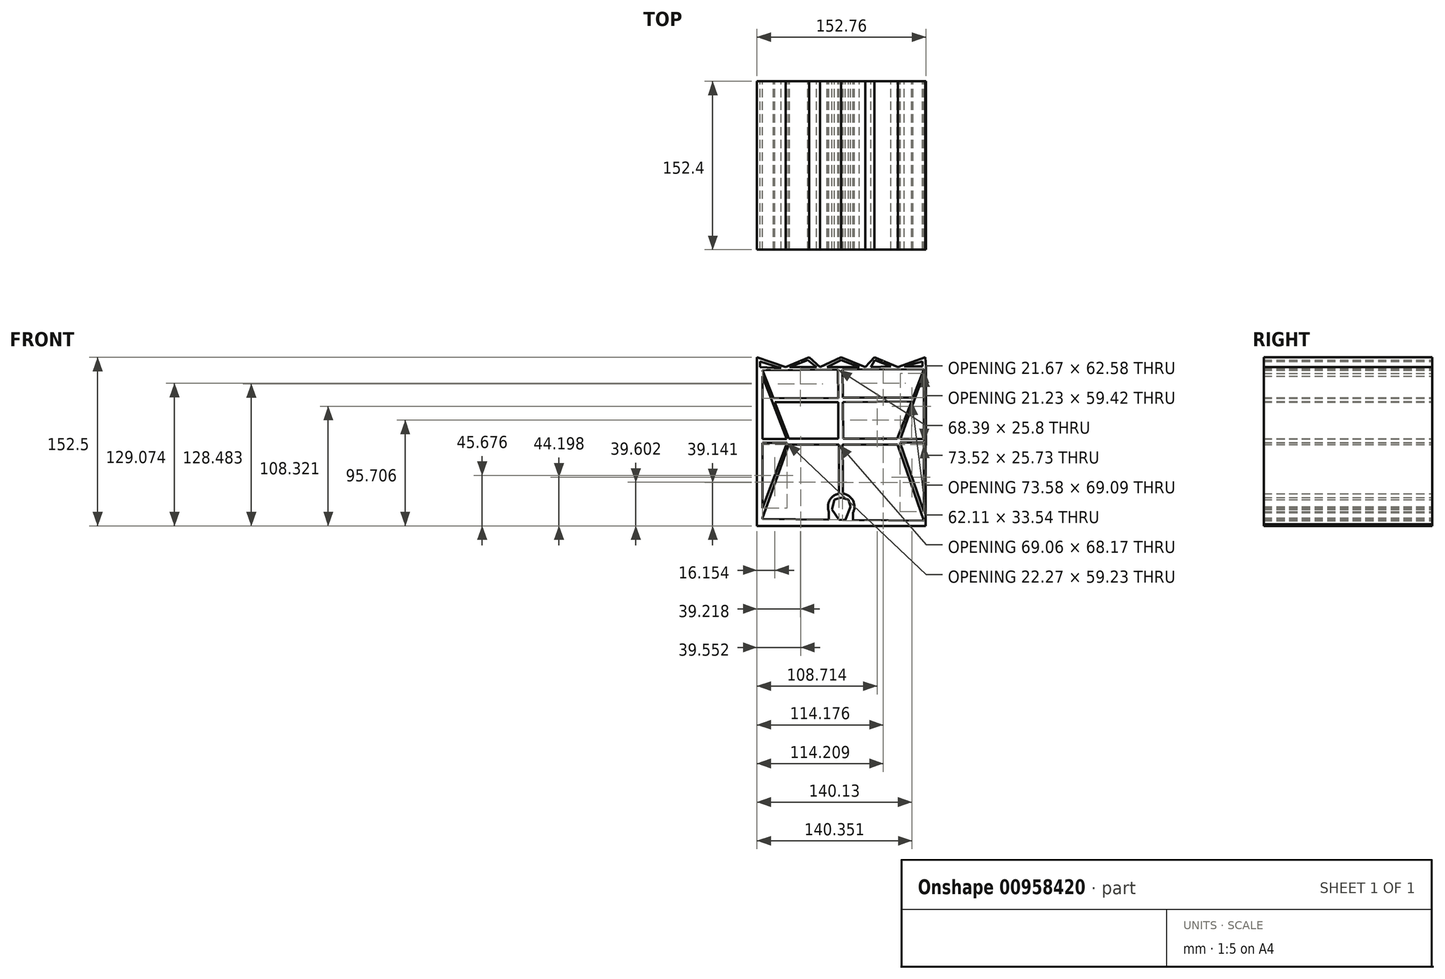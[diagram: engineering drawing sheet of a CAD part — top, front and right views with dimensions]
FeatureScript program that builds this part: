
annotation { "Feature Type Name" : "Feature", "Feature Type Description" : "" }
export const myFeature = defineFeature(function(context is Context, id is Id, definition is map)
    precondition{}
    {
        {
            var Q0;
            Q0=qCreatedBy(makeId("Front.planeOp"),FACE);
            var sketch = newSketch(context, id + "F0", { "sketchPlane" : qUnion([Q0])});
            skLineSegment(sketch, "E0", {"start": v(-71.15, 59.1) * mm, "end": v(-71.15, 2.17) * mm});
            skLineSegment(sketch, "E1", {"start": v(-71.15, -70.3) * mm, "end": v(-11.18, -70.94) * mm});
            skLineSegment(sketch, "E2", {"start": v(74.8, 65.48) * mm, "end": v(1.28, 64.96) * mm});
            skLineSegment(sketch, "E3", {"start": v(-71.15, 64.44) * mm, "end": v(-61.46, 39.21) * mm});
            skLineSegment(sketch, "E4", {"start": v(-47.38, -2.77) * mm, "end": v(-71.15, -69.26) * mm});
            skLineSegment(sketch, "E5", {"start": v(74.8, 65.48) * mm, "end": v(65.02, 39.75) * mm});
            skLineSegment(sketch, "E6", {"start": v(50.87, -2.77) * mm, "end": v(74.8, -71.87) * mm});
            skLineSegment(sketch, "E7", {"start": v(-71.15, 59.1) * mm, "end": v(-49.28, 2.17) * mm});
            skLineSegment(sketch, "E8", {"start": v(-48.88, -1.17) * mm, "end": v(-71.15, -60.4) * mm});
            skLineSegment(sketch, "E9", {"start": v(74.8, 61.57) * mm, "end": v(53.56, 2.17) * mm});
            skLineSegment(sketch, "E10", {"start": v(53.12, -0.97) * mm, "end": v(74.8, -63.55) * mm});
            skPoint(sketch, "E11.start.orphan", {"position": v(-69.1, -63.55) * mm});
            skLineSegment(sketch, "E12.trimOffspring", {"start": v(-71.15, -69.26) * mm, "end": v(-71.15, -70.3) * mm});
            skLineSegment(sketch, "E13.trimOffspring", {"start": v(74.8, -63.55) * mm, "end": v(74.8, -1) * mm});
            skLineSegment(sketch, "E14", {"start": v(-76.17, 67.36) * mm, "end": v(-76.17, -76.46) * mm});
            skLineSegment(sketch, "E15", {"start": v(-76.17, -76.46) * mm, "end": v(76.3, -76.46) * mm});
            skLineSegment(sketch, "E16", {"start": v(76.45, -74.92) * mm, "end": v(76.3, -76.46) * mm});
            skLineSegment(sketch, "E17", {"start": v(76.45, -74.92) * mm, "end": v(76.59, 67.36) * mm});
            skPoint(sketch, "E18.end.orphan", {"position": v(74.8, -68.33) * mm});
            skArc(sketch, "E19", {"start": v(10.66, -64.64) * mm, "mid": v(10.6, -53.5) * mm, "end": v(1.41, -47.21) * mm});
            skLineSegment(sketch, "E20", {"start": v(-2.09, -47.31) * mm, "end": v(-2.09, -30.61) * mm});
            skLineSegment(sketch, "E21", {"start": v(1.41, -30.61) * mm, "end": v(1.41, -47.21) * mm});
            skLineSegment(sketch, "E22", {"start": v(-2.09, -70.94) * mm, "end": v(-8.25, -61.78) * mm});
            skLineSegment(sketch, "E23", {"start": v(-8.25, -61.78) * mm, "end": v(-6.15, -52.84) * mm});
            skLineSegment(sketch, "E24", {"start": v(-6.15, -52.84) * mm, "end": v(0, -50.7) * mm});
            skLineSegment(sketch, "E25", {"start": v(0, -50.7) * mm, "end": v(6.43, -52.84) * mm});
            skLineSegment(sketch, "E26", {"start": v(6.43, -52.84) * mm, "end": v(8.6, -59.12) * mm});
            skLineSegment(sketch, "E27", {"start": v(8.6, -59.12) * mm, "end": v(3.63, -71.1) * mm});
            skLineSegment(sketch, "E28.trimOffspring", {"start": v(10.66, -71.18) * mm, "end": v(74.8, -71.87) * mm});
            skArc(sketch, "E29.trimOffspring", {"start": v(-2.09, -47.31) * mm, "mid": v(-10.46, -53.24) * mm, "end": v(-11.18, -63.47) * mm});
            skLineSegment(sketch, "E30", {"start": v(-71.15, 2.17) * mm, "end": v(-49.28, 2.17) * mm});
            skLineSegment(sketch, "E31", {"start": v(-48.88, -1.17) * mm, "end": v(-71.15, -1.17) * mm});
            skLineSegment(sketch, "E32.trimOffspring", {"start": v(-71.15, -1.17) * mm, "end": v(-71.15, -60.4) * mm});
            skPoint(sketch, "E33.orphan", {"position": v(-48.44, 0) * mm});
            skLineSegment(sketch, "E34", {"start": v(-11.18, -63.47) * mm, "end": v(-11.18, -70.94) * mm});
            skLineSegment(sketch, "E35", {"start": v(10.66, -64.64) * mm, "end": v(10.66, -71.18) * mm});
            skLineSegment(sketch, "E36", {"start": v(-2.09, -70.94) * mm, "end": v(3.63, -71.1) * mm});
            skLineSegment(sketch, "E37", {"start": v(53.56, 2.17) * mm, "end": v(74.8, 2.15) * mm});
            skLineSegment(sketch, "E38", {"start": v(74.8, -1) * mm, "end": v(53.12, -0.97) * mm});
            skLineSegment(sketch, "E39", {"start": v(-47.4, 2.63) * mm, "end": v(-2.5, 2.56) * mm});
            skLineSegment(sketch, "E40", {"start": v(-47.38, -2.77) * mm, "end": v(-2.09, -2.77) * mm});
            skPoint(sketch, "E41.orphan", {"position": v(-46.4, 0) * mm});
            skPoint(sketch, "E42.orphan", {"position": v(49.9, 0) * mm});
            skPoint(sketch, "E43.orphan", {"position": v(52.79, 0) * mm});
            skLineSegment(sketch, "E44.trimOffspring", {"start": v(74.8, 2.15) * mm, "end": v(74.8, 61.57) * mm});
            skLineSegment(sketch, "E45", {"start": v(-2.94, 64.93) * mm, "end": v(-2.75, 39.12) * mm});
            skLineSegment(sketch, "E46", {"start": v(1.73, 2.55) * mm, "end": v(1.49, 35.57) * mm});
            skLineSegment(sketch, "E47", {"start": v(-61.46, 39.21) * mm, "end": v(-2.75, 39.12) * mm});
            skLineSegment(sketch, "E48", {"start": v(-2.73, 35.57) * mm, "end": v(-60.06, 35.57) * mm});
            skLineSegment(sketch, "E49", {"start": v(1.41, -30.61) * mm, "end": v(1.21, -2.77) * mm});
            skLineSegment(sketch, "E50.trimOffspring", {"start": v(1.73, 2.55) * mm, "end": v(50.85, 2.48) * mm});
            skPoint(sketch, "E51.end.orphan", {"position": v(0, -27.12) * mm});
            skLineSegment(sketch, "E52.trimOffspring", {"start": v(-60.06, 35.57) * mm, "end": v(-47.4, 2.63) * mm});
            skLineSegment(sketch, "E53.trimOffspring", {"start": v(-2.73, 35.57) * mm, "end": v(-2.5, 2.56) * mm});
            skLineSegment(sketch, "E54.trimOffspring", {"start": v(-2.94, 64.93) * mm, "end": v(-71.15, 64.44) * mm});
            skLineSegment(sketch, "E55", {"start": v(-2.09, -30.61) * mm, "end": v(-2.09, -2.77) * mm});
            skLineSegment(sketch, "E56", {"start": v(1.46, 39.75) * mm, "end": v(65.02, 39.75) * mm});
            skLineSegment(sketch, "E57", {"start": v(1.49, 35.57) * mm, "end": v(63.6, 36.02) * mm});
            skLineSegment(sketch, "E58.trimOffspring", {"start": v(1.46, 39.75) * mm, "end": v(1.28, 64.96) * mm});
            skLineSegment(sketch, "E59.trimOffspring", {"start": v(63.6, 36.02) * mm, "end": v(50.85, 2.48) * mm});
            skLineSegment(sketch, "E60.trimOffspring", {"start": v(1.21, -2.77) * mm, "end": v(50.87, -2.77) * mm});
            skLineSegment(sketch, "E61", {"start": v(-76.17, 67.36) * mm, "end": v(-76.17, 76.04) * mm});
            skLineSegment(sketch, "E62", {"start": v(-76.17, 76.04) * mm, "end": v(-50.19, 67.36) * mm});
            skLineSegment(sketch, "E63", {"start": v(-50.19, 67.36) * mm, "end": v(-28.91, 76.04) * mm});
            skLineSegment(sketch, "E64", {"start": v(-28.91, 76.04) * mm, "end": v(-19.12, 67.36) * mm});
            skLineSegment(sketch, "E65", {"start": v(-19.12, 67.36) * mm, "end": v(0, 76.04) * mm});
            skLineSegment(sketch, "E66", {"start": v(0, 76.04) * mm, "end": v(21.73, 67.36) * mm});
            skLineSegment(sketch, "E67", {"start": v(21.73, 67.36) * mm, "end": v(29.95, 76.04) * mm});
            skLineSegment(sketch, "E68", {"start": v(29.95, 76.04) * mm, "end": v(51.36, 67.36) * mm});
            skLineSegment(sketch, "E69", {"start": v(51.36, 67.36) * mm, "end": v(76.16, 76.04) * mm});
            skLineSegment(sketch, "E70", {"start": v(76.16, 76.04) * mm, "end": v(76.59, 67.36) * mm});
            skLineSegment(sketch, "E71", {"start": v(-73.55, 67.36) * mm, "end": v(-73.55, 72.25) * mm});
            skLineSegment(sketch, "E72", {"start": v(-73.55, 72.25) * mm, "end": v(-54.5, 66.38) * mm});
            skLineSegment(sketch, "E73", {"start": v(-54.5, 66.38) * mm, "end": v(-73.55, 67.36) * mm});
            skLineSegment(sketch, "E74", {"start": v(-46.93, 67.36) * mm, "end": v(-30.22, 73.69) * mm});
            skLineSegment(sketch, "E75", {"start": v(-30.22, 73.69) * mm, "end": v(-22.39, 67.36) * mm});
            skLineSegment(sketch, "E76", {"start": v(-22.39, 67.36) * mm, "end": v(-46.93, 67.36) * mm});
            skLineSegment(sketch, "E77", {"start": v(-12.73, 67.36) * mm, "end": v(0, 73.69) * mm});
            skLineSegment(sketch, "E78", {"start": v(0, 73.69) * mm, "end": v(16.51, 67.36) * mm});
            skLineSegment(sketch, "E79", {"start": v(16.51, 67.36) * mm, "end": v(-12.73, 67.36) * mm});
            skLineSegment(sketch, "E80", {"start": v(26.82, 67.36) * mm, "end": v(30.35, 73.69) * mm});
            skLineSegment(sketch, "E81", {"start": v(30.35, 73.69) * mm, "end": v(44.95, 67.77) * mm});
            skLineSegment(sketch, "E82", {"start": v(44.95, 67.77) * mm, "end": v(26.82, 67.36) * mm});
            skLineSegment(sketch, "E83", {"start": v(57.1, 67.77) * mm, "end": v(73.68, 72.25) * mm});
            skLineSegment(sketch, "E84", {"start": v(73.68, 72.25) * mm, "end": v(73.71, 67.77) * mm});
            skLineSegment(sketch, "E85", {"start": v(73.71, 67.77) * mm, "end": v(57.1, 67.77) * mm});
            skSolve(sketch);
        }
        {
            var Q0;
            Q0 = qSketchRegion(id + "F0", true);
            extrude(context, id + "F1", {"entities" : qUnion([Q0]), "depth" : 152.4 * mm, "offsetDistance" : 25.4 * mm});
        }
    });
